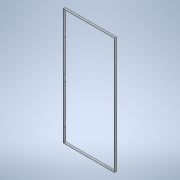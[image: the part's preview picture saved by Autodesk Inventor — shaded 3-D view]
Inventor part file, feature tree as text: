
AUTODESK INVENTOR PART (.ipt)
format: ipt  version: 2021 (Build 250183000, 183)  size: 138,752 bytes
history: native  units: mm
features: extrude x2, sketch x2
ambient origin geometry x8: Origin, YZ Plane, XZ Plane, XY Plane, X Axis, Y Axis, Z Axis, Center Point
bodies: Solid1 (feature_tree)
feature tree (4):
  extrude  "Extrusion1"  Depth=2100.0mm
  extrude  "Extrusion2"  Depth=40.0mm TaperAngle=0.0deg
  sketch  "Sketch1"  dims[d0=920.0mm d1=2100.0mm]
  sketch  "Sketch2"  dims[d2=4.0mm d3=40.0mm d4=0.0mm d5=100.0mm d7=30.0mm d9=700.0mm d10=10.0mm d12=10.0mm d14=2.5mm d15=0.0mm d16=350.0mm]
